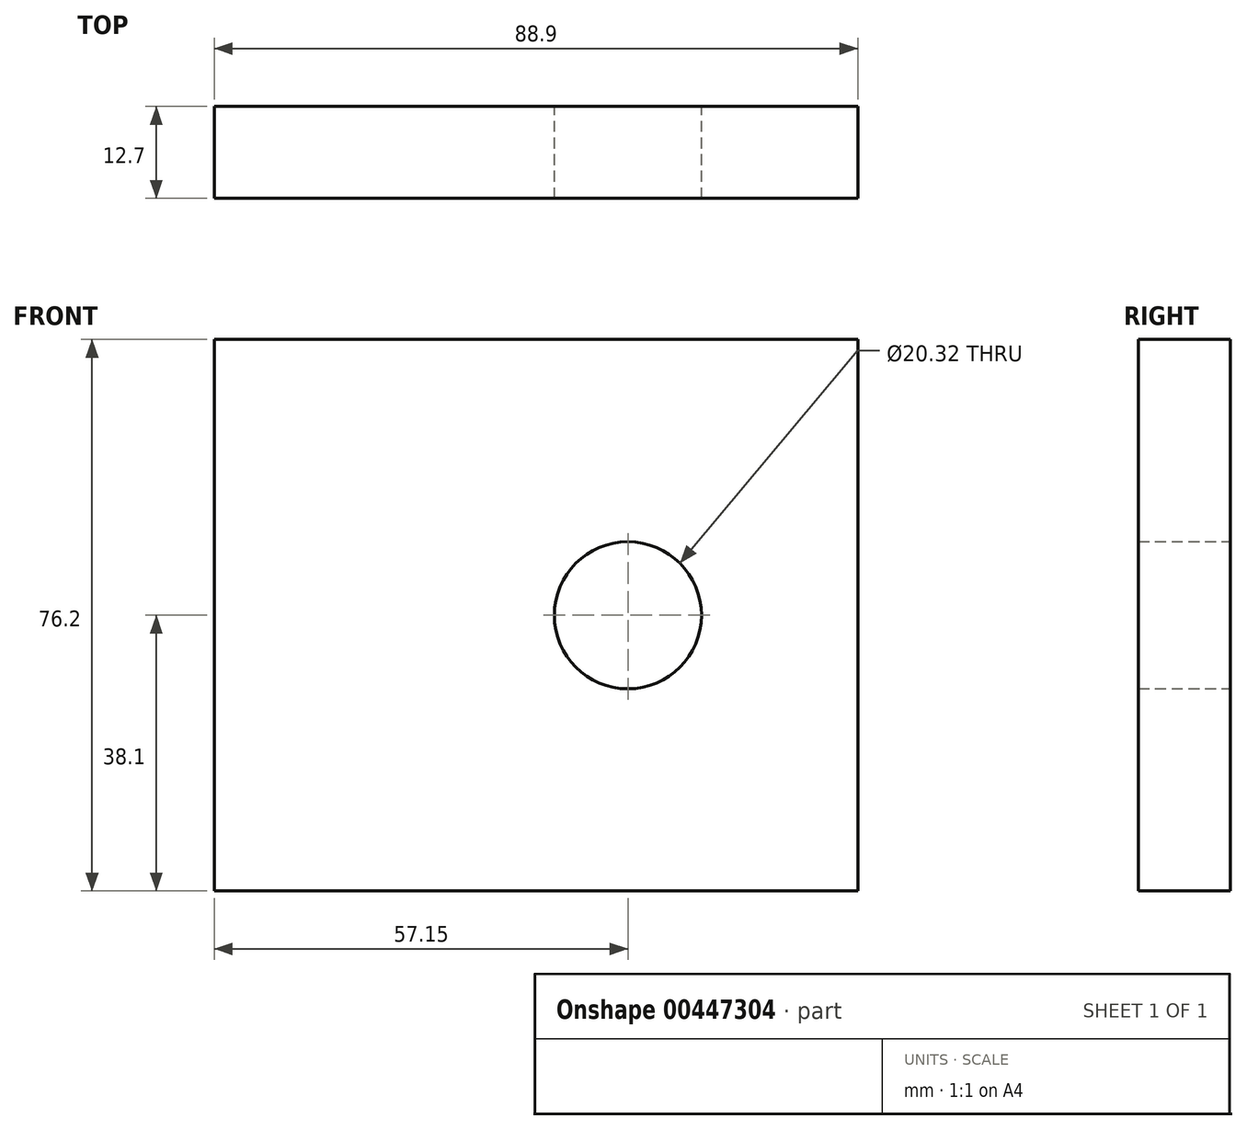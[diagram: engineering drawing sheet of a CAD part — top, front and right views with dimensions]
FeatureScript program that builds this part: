
annotation { "Feature Type Name" : "Feature", "Feature Type Description" : "" }
export const myFeature = defineFeature(function(context is Context, id is Id, definition is map)
    precondition{}
    {
        {
            var Q0;
            Q0=qCreatedBy(makeId("Front.planeOp"),FACE);
            var sketch = newSketch(context, id + "F0", { "sketchPlane" : qUnion([Q0])});
            skLineSegment(sketch, "E0.bottom", {"start": v(-44.45, -38.1) * mm, "end": v(44.45, -38.1) * mm});
            skLineSegment(sketch, "E0.top", {"start": v(-44.45, 38.1) * mm, "end": v(44.45, 38.1) * mm});
            skLineSegment(sketch, "E0.left", {"start": v(-44.45, -38.1) * mm, "end": v(-44.45, 38.1) * mm});
            skLineSegment(sketch, "E0.right", {"start": v(44.45, -38.1) * mm, "end": v(44.45, 38.1) * mm});
            skPoint(sketch, "E0.middle", {"position": v(0, 0) * mm});
            skPoint(sketch, "E1", {"position": v(12.7, 0) * mm});
            skSolve(sketch);
        }
        {
            var Q0;
            Q0=makeQuery(id+"F0.imprint","IMPRINT",FACE,{"disambiguationData":[TD([[makeQuery(id+"F0.imprint","IMPRINT",EDGE,{"derivedFrom":sQuery(id+"F0.wireOp",EDGE,"E0.bottom")}),1.0]])]});
            extrude(context, id + "F1", {"entities" : qUnion([Q0]), "depth" : 12.7 * mm});
        }
        {
            var Q0;
            Q0=sQuery(id+"F0.wireOp",VERTEX,"E1");
            var Q1;
            Q1=makeQuery(id+"F1.opExtrude","SWEPT_BODY",BODY,{"disambiguationData":[OSD([sQuery(id+"F0.wireOp",EDGE,"E0.bottom"),sQuery(id+"F0.wireOp",EDGE,"E0.top"),sQuery(id+"F0.wireOp",EDGE,"E0.left"),sQuery(id+"F0.wireOp",EDGE,"E0.right")])]});
            hole(context, id + "F2", {"style" : HoleStyle.SIMPLE, "endStyle" : HoleEndStyle.THROUGH, "oppositeDirection" : true, "holeDiameter" : 20.32 * mm, "isTappedThrough" : true, "tappedDepth" : 12.7 * mm, "tapClearance" : 3, "locations" : qUnion([Q0]), "scope" : qUnion([Q1])});
        }
    });
